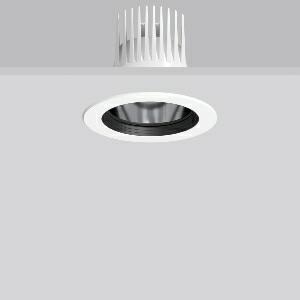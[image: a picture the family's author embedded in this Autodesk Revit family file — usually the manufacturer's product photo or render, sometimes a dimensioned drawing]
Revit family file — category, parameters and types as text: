
# Revit family: heledon_maxi_e_901758_002_1_76_3e2a
name_source: partatom
category: Lighting Fixtures
units: mm (PartAtom-declared; Revit-internal decimal feet)

## family parameters
Cut with Voids When Loaded = No
Host = Face
Light Source = No
Part Type = Normal
Room Calculation Point = No
Round Connector Dimension = Use Diameter
Shared = No

## types (1)
- HELEDON maxi E (1 x LED Modul 940, 3500 lm, 4000)
    Apparent Load = 25 VA
    Approval mark = CE
    CIE Flux Codes = 100 100 100 100 100
    Color Rendering = 92
    Color Temperature = 4000
    Default Elevation = 1800 mm
    Description = Series: HELEDON maxi
Round recessed downlight. Housing: die-cast aluminium, powder-coated. Black plastic ring and recessed LED to prevent glare from the side. Optical assembly with reflector made of MIRO-Silver with 98% total light reflection for outstanding efficiency - can be changed without tools. Best colour rendering index Ra>90. Suitable for Recessed ceiling mounting. Installation without tools thanks to spring fastening system. Including separate LED converter with connecting cable 600 mm.High quality converter without flickering and stroboscopic effect. Through-wiring box (5 pole) available as accessory. The following accessories can be mounted without use of tools: interchangeable lenses, decorative glasses, honeycomb louvre, clear and frosted diffusers, white interchangeable plastic ring. 
Colour: traffic white, matt (RAL 9016)
Diameter: 162 mm
Height: 3 mm
Cut-out diameter: 152 mm
Recess height: 200 mm
Luminaire: recess height: 135 mm
Lamp: LED
Socket: without socket
Colour temperature: 4000K
Colour rendering index (CRI): 92
System power: 25 W
Rated luminous flux: 3500 lm
Luminous efficiency: 140 lm/W
Control gear: Converter, dimmable, DALI
Protection class: II
Type of protection: IP 20
    Height = 0 mm  [stored 0 ft]
    Lamp = 1 x LED Modul 940
    Lamp Light Flux = 3500 lm
    Lamp count = 1
    Length = 162 mm
    Lifetime = 50000 h
    Luminous efficacy = 140 lm/W
    Manufacturer = RZB
    ModVariant = No
    Model = 901758.002.1.76
    Mounting Place = Ceiling
    Mounting Type = Recessed
    Number of Poles = 1
    OnlyDefault = Yes
    Power Factor = 1
    Product Name = HELEDON maxi E
    Product group = Recessed downlights
    ProductGroupID = 402
    Protection Class = Protection class II
    Protection Degree = IP 20
    RLX_Detail_Level = 1
    RLX_Emergency_Light_Flux = 0 lm
    RLX_Emergency_Type = 0
    RLX_Emergency_Type_DB = No
    RlxData = <blob elided: 119193 chars, md5=41c6defa>
    Socket = socket
    Standby Power = 0 W
    System Light Flux = 3500 lm
    System Power = 25 W
    Type Comments = Product without accessories
    Type Image = 901662.002.jpg
    URL = http://relux.com
    VarID = ---
    Voltage = 230 V
    Voltage Range = 220-240 V
    Weight = 0.00 kg
    Width = 0 mm  [stored 0 ft]

note: [stored X ft] marks values corroborated as IEEE doubles in the binary element streams (Revit-internal decimal feet)

## geometry (parser evidence)
native form markers: Blend x4, Sweep x11
no freeform markers — native parametric forms only
